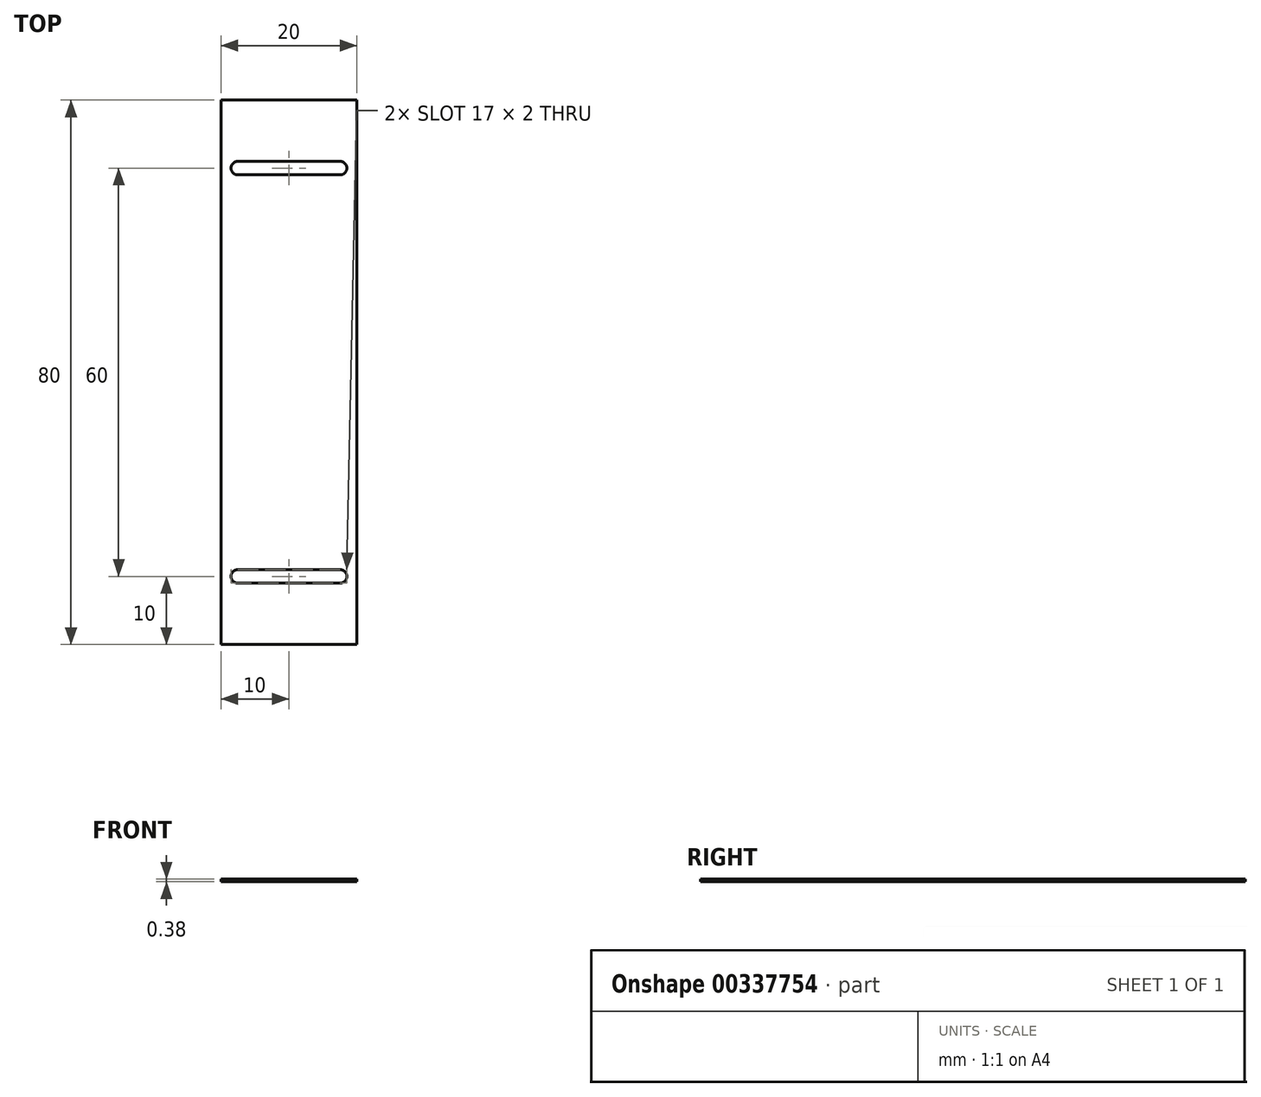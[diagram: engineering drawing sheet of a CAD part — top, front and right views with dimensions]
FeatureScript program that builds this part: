
annotation { "Feature Type Name" : "Feature", "Feature Type Description" : "" }
export const myFeature = defineFeature(function(context is Context, id is Id, definition is map)
    precondition{}
    {
        {
            var Q0;
            Q0=qCreatedBy(makeId("Front.planeOp"),FACE);
            var sketch = newSketch(context, id + "F0", { "sketchPlane" : qUnion([Q0])});
            skLineSegment(sketch, "E0.bottom", {"start": v(10, -0.2) * mm, "end": v(-10, -0.2) * mm});
            skLineSegment(sketch, "E0.top", {"start": v(10, 0.2) * mm, "end": v(-10, 0.2) * mm});
            skLineSegment(sketch, "E0.left", {"start": v(10, -0.2) * mm, "end": v(10, 0.2) * mm});
            skLineSegment(sketch, "E0.right", {"start": v(-10, -0.2) * mm, "end": v(-10, 0.2) * mm});
            skPoint(sketch, "E0.middle", {"position": v(0, 0) * mm});
            skSolve(sketch);
        }
        {
            var Q0;
            Q0 = qSketchRegion(id + "F0", true);
            extrude(context, id + "F1", {"entities" : qUnion([Q0]), "depth" : 80 * mm});
        }
        {
            var Q0;
            Q0=makeQuery(id+"F1.opExtrude","SWEPT_FACE",FACE,{"disambiguationData":[OSD([sQuery(id+"F0.wireOp",EDGE,"E0.top")])]});
            var sketch = newSketch(context, id + "F2", { "sketchPlane" : qUnion([Q0])});
            skLineSegment(sketch, "E1", {"start": v(-7.5, -10) * mm, "end": v(7.5, -10) * mm});
            skLineSegment(sketch, "E2", {"start": v(-7.5, -70) * mm, "end": v(7.5, -70) * mm});
            skArc(sketch, "E3.0.startCap", {"start": v(-7.5, -11) * mm, "mid": v(-8.5, -10) * mm, "end": v(-7.5, -9) * mm});
            skArc(sketch, "E3.0.endCap", {"start": v(7.5, -9) * mm, "mid": v(8.5, -10) * mm, "end": v(7.5, -11) * mm});
            skLineSegment(sketch, "E3.0.left", {"start": v(-7.5, -9) * mm, "end": v(7.5, -9) * mm});
            skLineSegment(sketch, "E3.0.right", {"start": v(-7.5, -11) * mm, "end": v(7.5, -11) * mm});
            skArc(sketch, "E3.1.startCap", {"start": v(-7.5, -71) * mm, "mid": v(-8.5, -70) * mm, "end": v(-7.5, -69) * mm});
            skArc(sketch, "E3.1.endCap", {"start": v(7.5, -69) * mm, "mid": v(8.5, -70) * mm, "end": v(7.5, -71) * mm});
            skLineSegment(sketch, "E3.1.left", {"start": v(-7.5, -69) * mm, "end": v(7.5, -69) * mm});
            skLineSegment(sketch, "E3.1.right", {"start": v(-7.5, -71) * mm, "end": v(7.5, -71) * mm});
            skSolve(sketch);
        }
        {
            var Q0;
            Q0 = qSketchRegion(id + "F2", true);
            extrude(context, id + "F3", {"entities" : qUnion([Q0]), "operationType" : NewBodyOperationType.REMOVE, "oppositeDirection" : true, "depth" : 25 * mm});
        }
    });
